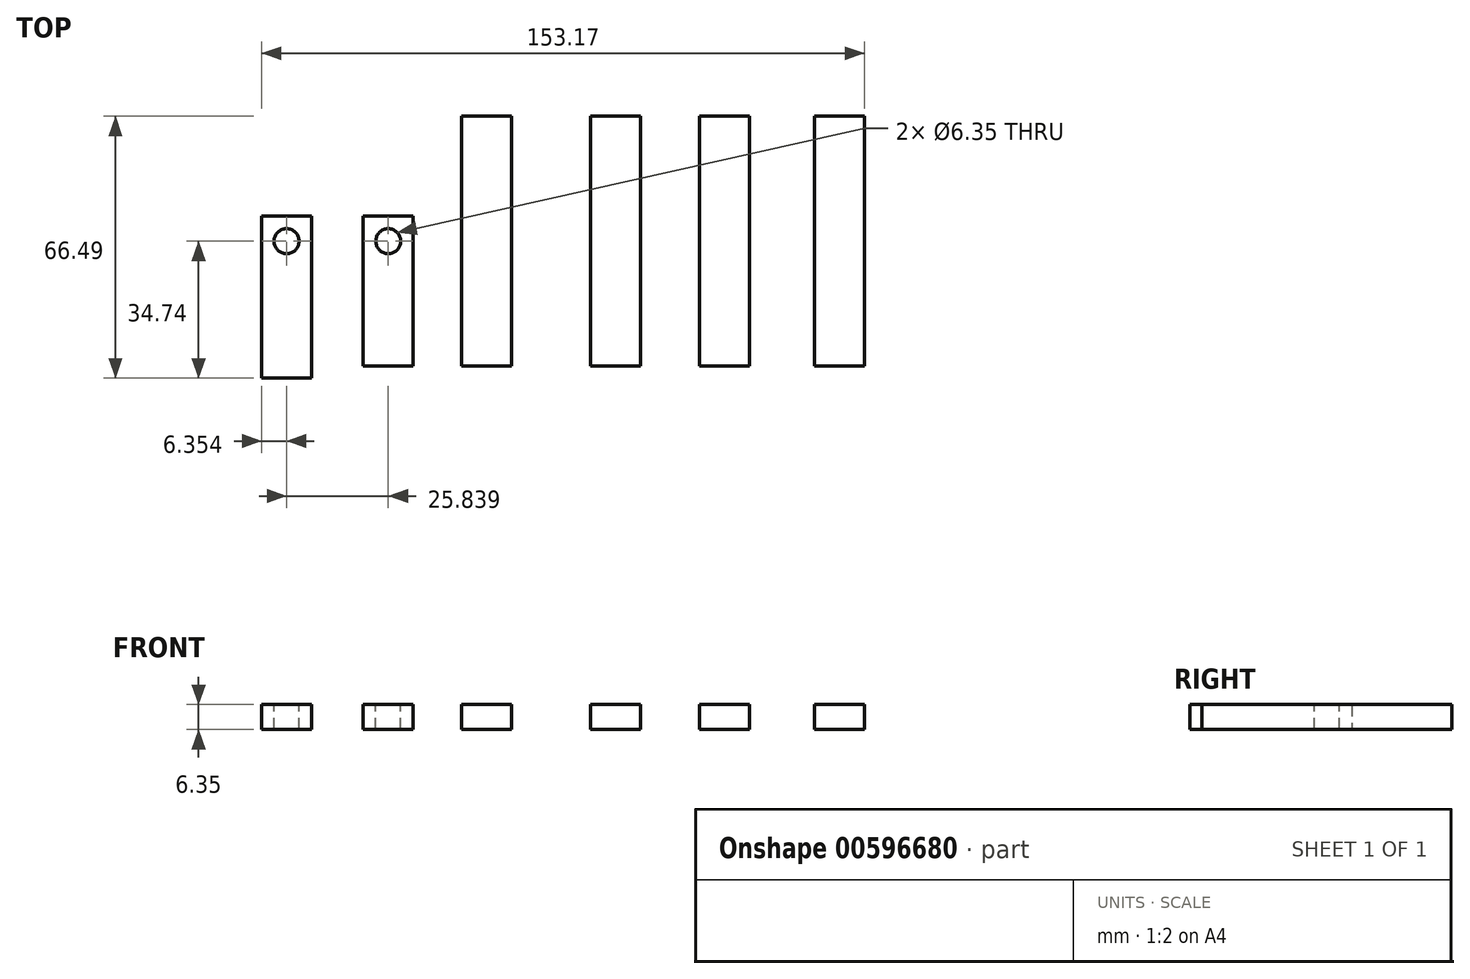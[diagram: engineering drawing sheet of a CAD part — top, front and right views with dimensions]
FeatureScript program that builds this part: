
annotation { "Feature Type Name" : "Feature", "Feature Type Description" : "" }
export const myFeature = defineFeature(function(context is Context, id is Id, definition is map)
    precondition{}
    {
        {
            var Q0;
            Q0=qCreatedBy(makeId("Top.planeOp"),FACE);
            var sketch = newSketch(context, id + "F0", { "sketchPlane" : qUnion([Q0])});
            skLineSegment(sketch, "E0.bottom", {"start": v(0, 0) * mm, "end": v(12.7, 0) * mm});
            skLineSegment(sketch, "E0.top", {"start": v(0, 63.5) * mm, "end": v(12.7, 63.5) * mm});
            skLineSegment(sketch, "E0.left", {"start": v(0, 0) * mm, "end": v(0, 63.5) * mm});
            skLineSegment(sketch, "E0.right", {"start": v(12.7, 0) * mm, "end": v(12.7, 63.5) * mm});
            skLineSegment(sketch, "E1.bottom", {"start": v(27.73, 0) * mm, "end": v(40.43, 0) * mm});
            skLineSegment(sketch, "E1.top", {"start": v(27.73, 63.5) * mm, "end": v(40.43, 63.5) * mm});
            skLineSegment(sketch, "E1.left", {"start": v(27.73, 0) * mm, "end": v(27.73, 63.5) * mm});
            skLineSegment(sketch, "E1.right", {"start": v(40.43, 0) * mm, "end": v(40.43, 63.5) * mm});
            skLineSegment(sketch, "E2.bottom", {"start": v(56.9, 0) * mm, "end": v(69.6, 0) * mm});
            skLineSegment(sketch, "E2.top", {"start": v(56.9, 63.5) * mm, "end": v(69.6, 63.5) * mm});
            skLineSegment(sketch, "E2.left", {"start": v(56.9, 0) * mm, "end": v(56.9, 63.5) * mm});
            skLineSegment(sketch, "E2.right", {"start": v(69.6, 0) * mm, "end": v(69.6, 63.5) * mm});
            skPoint(sketch, "E3.firstSnap0", {"position": v(6.35, 0) * mm});
            skLineSegment(sketch, "E3.bottom", {"start": v(-57.73, 0) * mm, "end": v(-45.03, 0) * mm});
            skLineSegment(sketch, "E3.top", {"start": v(-57.73, 38.1) * mm, "end": v(-45.03, 38.1) * mm});
            skLineSegment(sketch, "E3.left", {"start": v(-57.73, 0) * mm, "end": v(-57.73, 38.1) * mm});
            skLineSegment(sketch, "E3.right", {"start": v(-45.03, 0) * mm, "end": v(-45.03, 38.1) * mm});
            skLineSegment(sketch, "E4.bottom", {"start": v(-32.78, 0) * mm, "end": v(-20.08, 0) * mm});
            skLineSegment(sketch, "E4.top", {"start": v(-32.78, 63.5) * mm, "end": v(-20.08, 63.5) * mm});
            skLineSegment(sketch, "E4.left", {"start": v(-32.78, 0) * mm, "end": v(-32.78, 63.5) * mm});
            skLineSegment(sketch, "E4.right", {"start": v(-20.08, 0) * mm, "end": v(-20.08, 63.5) * mm});
            skLineSegment(sketch, "E5.bottom", {"start": v(-83.57, 0) * mm, "end": v(-70.87, 0) * mm});
            skLineSegment(sketch, "E5.top", {"start": v(-83.57, 38.1) * mm, "end": v(-70.87, 38.1) * mm});
            skLineSegment(sketch, "E5.left", {"start": v(-83.57, 0) * mm, "end": v(-83.57, 38.1) * mm});
            skLineSegment(sketch, "E5.right", {"start": v(-70.87, 0) * mm, "end": v(-70.87, 38.1) * mm});
            skSolve(sketch);
        }
        {
            var Q0;
            Q0=makeQuery(id+"F0.imprint","IMPRINT",FACE,{"disambiguationData":[TD([[makeQuery(id+"F0.imprint","IMPRINT",EDGE,{"derivedFrom":sQuery(id+"F0.wireOp",EDGE,"E5.bottom")}),1.0]])]});
            var Q1;
            Q1=makeQuery(id+"F0.imprint","IMPRINT",FACE,{"disambiguationData":[TD([[makeQuery(id+"F0.imprint","IMPRINT",EDGE,{"derivedFrom":sQuery(id+"F0.wireOp",EDGE,"E3.bottom")}),1.0]])]});
            var Q2;
            Q2=makeQuery(id+"F0.imprint","IMPRINT",FACE,{"disambiguationData":[TD([[makeQuery(id+"F0.imprint","IMPRINT",EDGE,{"derivedFrom":sQuery(id+"F0.wireOp",EDGE,"E4.bottom")}),1.0]])]});
            var Q3;
            Q3=makeQuery(id+"F0.imprint","IMPRINT",FACE,{"disambiguationData":[TD([[makeQuery(id+"F0.imprint","IMPRINT",EDGE,{"derivedFrom":sQuery(id+"F0.wireOp",EDGE,"E0.bottom")}),1.0]])]});
            var Q4;
            Q4=makeQuery(id+"F0.imprint","IMPRINT",FACE,{"disambiguationData":[TD([[makeQuery(id+"F0.imprint","IMPRINT",EDGE,{"derivedFrom":sQuery(id+"F0.wireOp",EDGE,"E1.bottom")}),1.0]])]});
            var Q5;
            Q5=makeQuery(id+"F0.imprint","IMPRINT",FACE,{"disambiguationData":[TD([[makeQuery(id+"F0.imprint","IMPRINT",EDGE,{"derivedFrom":sQuery(id+"F0.wireOp",EDGE,"E2.bottom")}),1.0]])]});
            extrude(context, id + "F1", {"entities" : qUnion([Q0, Q1, Q2, Q3, Q4, Q5]), "depth" : 6.35 * mm, "offsetDistance" : 25.4 * mm});
        }
        {
            var Q0;
            Q0=makeQuery(id+"F1.opExtrude","CAP_FACE",FACE,{"disambiguationData":[OSD([sQuery(id+"F0.wireOp",EDGE,"E5.bottom"),sQuery(id+"F0.wireOp",EDGE,"E5.top"),sQuery(id+"F0.wireOp",EDGE,"E5.left"),sQuery(id+"F0.wireOp",EDGE,"E5.right")])],"isStart":false});
            var sketch = newSketch(context, id + "F2", { "sketchPlane" : qUnion([Q0])});
            skLineSegment(sketch, "E6", {"start": v(-77.22, 38.1) * mm, "end": v(-77.22, 31.75) * mm});
            skSolve(sketch);
        }
        {
            var Q0;
            Q0=sQuery(id+"F2.wireOp",VERTEX,"E6.end");
            var Q1;
            Q1=makeQuery(id+"F1.opExtrude","SWEPT_BODY",BODY,{"disambiguationData":[OSD([sQuery(id+"F0.wireOp",EDGE,"E5.bottom"),sQuery(id+"F0.wireOp",EDGE,"E5.top"),sQuery(id+"F0.wireOp",EDGE,"E5.left"),sQuery(id+"F0.wireOp",EDGE,"E5.right")])]});
            hole(context, id + "F3", {"style" : HoleStyle.SIMPLE, "endStyle" : HoleEndStyle.BLIND, "holeDiameter" : 6.35 * mm, "majorDiameter" : 6.35 * mm, "holeDepth" : 63.5 * mm, "isTappedThrough" : true, "tappedDepth" : 12.7 * mm, "tapClearance" : 3, "locations" : qUnion([Q0]), "scope" : qUnion([Q1])});
        }
        {
            var Q0;
            Q0=makeQuery(id+"F1.opExtrude","CAP_FACE",FACE,{"disambiguationData":[OSD([sQuery(id+"F0.wireOp",EDGE,"E3.bottom"),sQuery(id+"F0.wireOp",EDGE,"E3.top"),sQuery(id+"F0.wireOp",EDGE,"E3.left"),sQuery(id+"F0.wireOp",EDGE,"E3.right")])],"isStart":false});
            var sketch = newSketch(context, id + "F4", { "sketchPlane" : qUnion([Q0])});
            skLineSegment(sketch, "E7", {"start": v(-51.38, 38.1) * mm, "end": v(-51.38, 31.75) * mm});
            skSolve(sketch);
        }
        {
            var Q0;
            Q0=sQuery(id+"F4.wireOp",VERTEX,"E7.end");
            var Q1;
            Q1=makeQuery(id+"F1.opExtrude","SWEPT_BODY",BODY,{"disambiguationData":[OSD([sQuery(id+"F0.wireOp",EDGE,"E3.bottom"),sQuery(id+"F0.wireOp",EDGE,"E3.top"),sQuery(id+"F0.wireOp",EDGE,"E3.left"),sQuery(id+"F0.wireOp",EDGE,"E3.right")])]});
            hole(context, id + "F5", {"style" : HoleStyle.SIMPLE, "endStyle" : HoleEndStyle.BLIND, "holeDiameter" : 6.35 * mm, "majorDiameter" : 6.35 * mm, "holeDepth" : 63.5 * mm, "isTappedThrough" : true, "tappedDepth" : 12.7 * mm, "tapClearance" : 3, "locations" : qUnion([Q0]), "scope" : qUnion([Q1])});
        }
        {
            var Q0;
            Q0=makeQuery(id+"F1.opExtrude","CAP_FACE",FACE,{"disambiguationData":[OSD([sQuery(id+"F0.wireOp",EDGE,"E5.bottom"),sQuery(id+"F0.wireOp",EDGE,"E5.top"),sQuery(id+"F0.wireOp",EDGE,"E5.left"),sQuery(id+"F0.wireOp",EDGE,"E5.right")])],"isStart":false});
            var sketch = newSketch(context, id + "F6", { "sketchPlane" : qUnion([Q0])});
            skLineSegment(sketch, "E8", {"start": v(-83.57, 0) * mm, "end": v(-83.57, -2.99) * mm});
            skLineSegment(sketch, "E9", {"start": v(-83.57, -2.99) * mm, "end": v(-70.87, -2.99) * mm});
            skLineSegment(sketch, "E10", {"start": v(-70.87, -2.99) * mm, "end": v(-70.87, 0) * mm});
            skLineSegment(sketch, "E11", {"start": v(-83.57, 0) * mm, "end": v(-70.87, 0) * mm});
            skSolve(sketch);
        }
        {
            var Q0;
            Q0=makeQuery(id+"F6.imprint","IMPRINT",FACE,{"disambiguationData":[TD([[makeQuery(id+"F6.imprint","IMPRINT",EDGE,{"derivedFrom":sQuery(id+"F6.wireOp",EDGE,"E8")}),1.0]])]});
            extrude(context, id + "F7", {"entities" : qUnion([Q0]), "operationType" : NewBodyOperationType.ADD, "oppositeDirection" : true, "depth" : 6.35 * mm, "offsetDistance" : 25.4 * mm});
        }
    });
